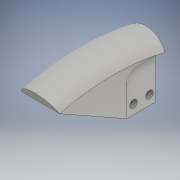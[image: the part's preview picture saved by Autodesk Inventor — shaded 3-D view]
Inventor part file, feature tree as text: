
AUTODESK INVENTOR PART (.ipt)
format: ipt  version: 2016 (Build 200138000, 138)  size: 934,400 bytes
history: native  units: in
note: dims shown in document units (in); Inventor stores cm internally (conversion verified against a paired STEP export)
features: sketch x5, extrude x2, other x2, hole x1, sweep x1, loft x1
ambient origin geometry x8: Origin, YZ Plane, XZ Plane, XY Plane, X Axis, Y Axis, Z Axis, Center Point
bodies: Solid1 (feature_tree)
feature tree (12):
  extrude  "Extrusion1"  Depth=0.5in
  extrude  "Extrusion2"  Depth=0.5in TaperAngle=0.0deg
  sketch  "Sketch4"  dims[d22=0.75in d23=0.0in d25=0.0125in]
  sketch  "Sketch6"  dims[d34=0.1575in d35=0.75in d36=0.1969in d37=0.1181in d38=0.5635in d39=1.0in d40=0.8108in d41=1.0in]
  hole  "Hole3"  [1 undecoded]
  sweep  "Sweep3"
  loft  "Loft1"
  sketch  "Sketch1"  dims[d0=0.75in d1=0.5in]
  sketch  "Sketch3"  dims[d2=0.4173in d3=0.5in d4=0.0in]
  sketch  "Sketch8"  dims[d42=0.0in d43=0.0in d44=0.0in d45=90.0deg d46=0.0in d47=90.0deg d5=1.0in d6=1.0in]
  other  "Edges1"
  other  "Edges2"
note: 1 required parameter value undecoded (feature->parameter linkage not recoverable at this tier; creation-order binding heuristic only, values carry confidence <= 0.55)
